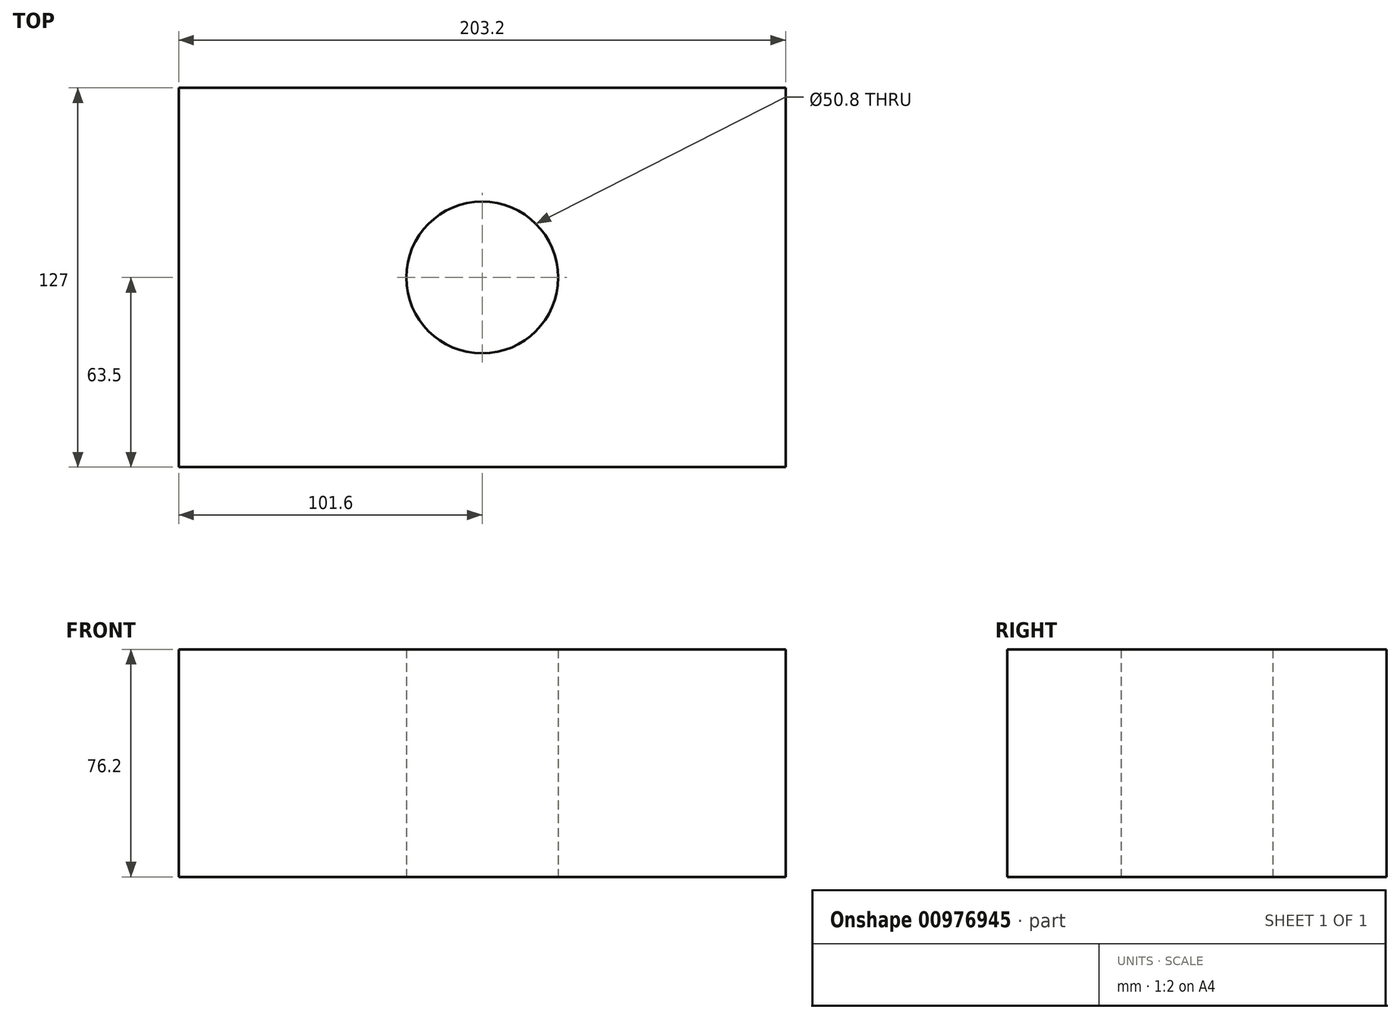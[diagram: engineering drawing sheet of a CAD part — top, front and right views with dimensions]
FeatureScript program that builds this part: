
annotation { "Feature Type Name" : "Feature", "Feature Type Description" : "" }
export const myFeature = defineFeature(function(context is Context, id is Id, definition is map)
    precondition{}
    {
        {
            var Q0;
            Q0=qCreatedBy(makeId("Top.planeOp"),FACE);
            var sketch = newSketch(context, id + "F0", { "sketchPlane" : qUnion([Q0])});
            skLineSegment(sketch, "E0.bottom", {"start": v(101.6, 63.5) * mm, "end": v(-101.6, 63.5) * mm});
            skLineSegment(sketch, "E0.top", {"start": v(101.6, -63.5) * mm, "end": v(-101.6, -63.5) * mm});
            skLineSegment(sketch, "E0.left", {"start": v(101.6, 63.5) * mm, "end": v(101.6, -63.5) * mm});
            skLineSegment(sketch, "E0.right", {"start": v(-101.6, 63.5) * mm, "end": v(-101.6, -63.5) * mm});
            skPoint(sketch, "E0.middle", {"position": v(0, 0) * mm});
            skCircle(sketch, "E1", {"center": v(0, 0) * mm, "radius": 25.4 * mm});
            skSolve(sketch);
        }
        {
            var Q0;
            Q0=makeQuery(id+"F0.imprint","IMPRINT",FACE,{"disambiguationData":[TD([[makeQuery(id+"F0.imprint","IMPRINT",EDGE,{"derivedFrom":sQuery(id+"F0.wireOp",EDGE,"E0.bottom")}),1.0]])]});
            extrude(context, id + "F1", {"entities" : qUnion([Q0]), "depth" : 76.2 * mm, "offsetDistance" : 25.4 * mm});
        }
    });
